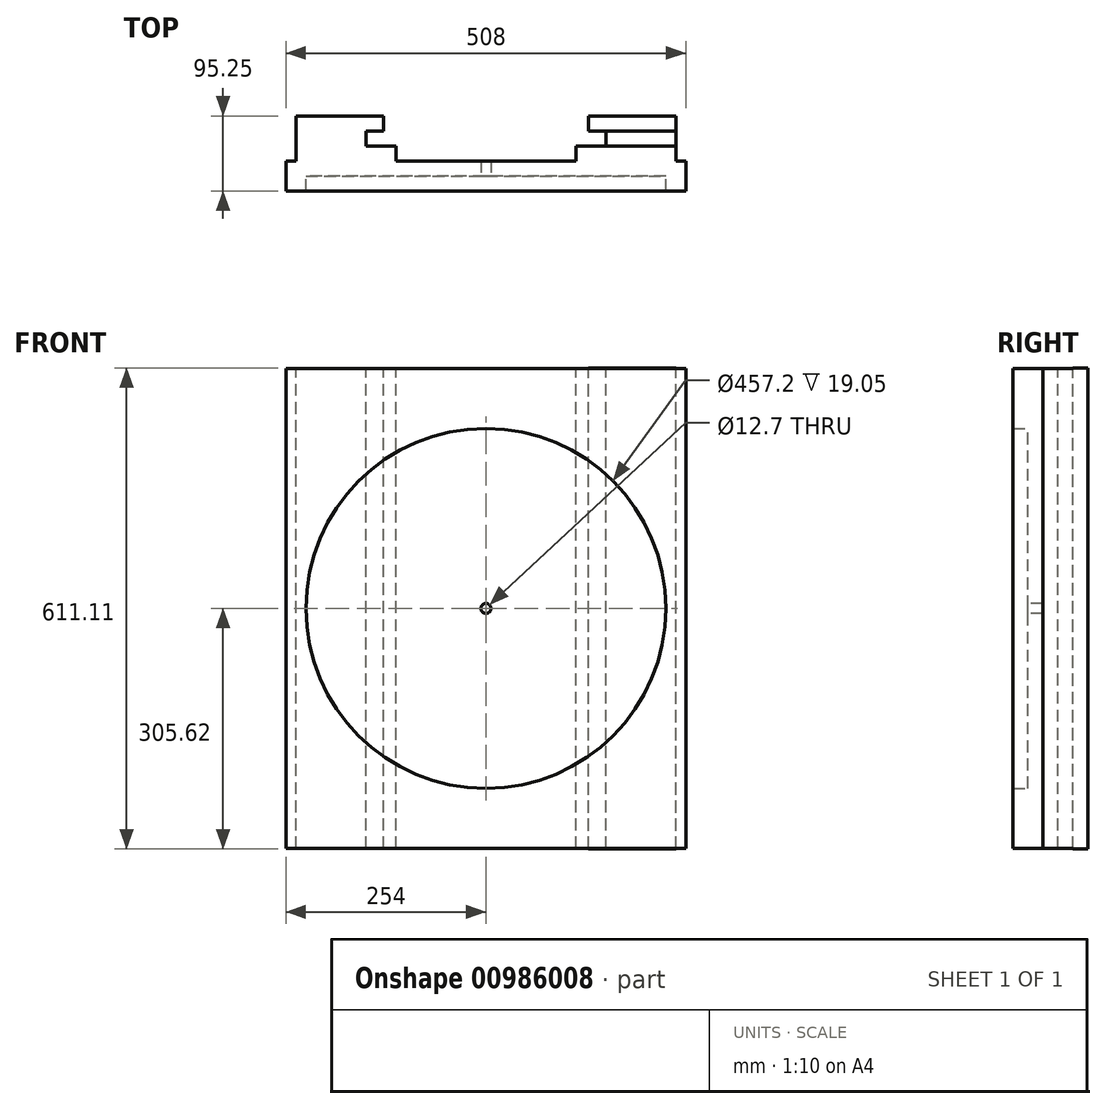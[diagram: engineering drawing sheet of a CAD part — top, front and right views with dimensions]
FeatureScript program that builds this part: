
annotation { "Feature Type Name" : "Feature", "Feature Type Description" : "" }
export const myFeature = defineFeature(function(context is Context, id is Id, definition is map)
    precondition{}
    {
        {
            var Q0;
            Q0=qCreatedBy(makeId("Front.planeOp"),FACE);
            var sketch = newSketch(context, id + "F0", { "sketchPlane" : qUnion([Q0])});
            skLineSegment(sketch, "E0.bottom", {"start": v(254, -304.8) * mm, "end": v(-254, -304.8) * mm});
            skLineSegment(sketch, "E0.top", {"start": v(254, 304.8) * mm, "end": v(-254, 304.8) * mm});
            skLineSegment(sketch, "E0.left", {"start": v(254, -304.8) * mm, "end": v(254, 304.8) * mm});
            skLineSegment(sketch, "E0.right", {"start": v(-254, -304.8) * mm, "end": v(-254, 304.8) * mm});
            skPoint(sketch, "E0.middle", {"position": v(0, 0) * mm});
            skSolve(sketch);
        }
        {
            var Q0;
            Q0 = qSketchRegion(id + "F0", true);
            extrude(context, id + "F1", {"entities" : qUnion([Q0]), "depth" : 19.05 * mm, "offsetDistance" : 25.4 * mm});
        }
        {
            var Q0;
            Q0=makeQuery(id+"F1.opExtrude","CAP_FACE",FACE,{"disambiguationData":[OSD([sQuery(id+"F0.wireOp",EDGE,"E0.bottom"),sQuery(id+"F0.wireOp",EDGE,"E0.top"),sQuery(id+"F0.wireOp",EDGE,"E0.left"),sQuery(id+"F0.wireOp",EDGE,"E0.right")])],"isStart":true});
            var sketch = newSketch(context, id + "F2", { "sketchPlane" : qUnion([Q0])});
            skLineSegment(sketch, "E1.bottom", {"start": v(-241.3, -304.8) * mm, "end": v(-114.3, -304.8) * mm});
            skLineSegment(sketch, "E1.top", {"start": v(-241.3, 304.8) * mm, "end": v(-114.3, 304.8) * mm});
            skLineSegment(sketch, "E1.left", {"start": v(-241.3, -304.8) * mm, "end": v(-241.3, 304.8) * mm});
            skLineSegment(sketch, "E1.right", {"start": v(-114.3, -304.8) * mm, "end": v(-114.3, 304.8) * mm});
            skLineSegment(sketch, "E2.bottom", {"start": v(114.3, -304.8) * mm, "end": v(241.3, -304.8) * mm});
            skLineSegment(sketch, "E2.top", {"start": v(114.3, 304.8) * mm, "end": v(241.3, 304.8) * mm});
            skLineSegment(sketch, "E2.left", {"start": v(114.3, -304.8) * mm, "end": v(114.3, 304.8) * mm});
            skLineSegment(sketch, "E2.right", {"start": v(241.3, -304.8) * mm, "end": v(241.3, 304.8) * mm});
            skSolve(sketch);
        }
        {
            var Q0;
            Q0=makeQuery(id+"F2.imprint","IMPRINT",FACE,{"disambiguationData":[TD([[makeQuery(id+"F2.imprint","IMPRINT",EDGE,{"derivedFrom":sQuery(id+"F2.wireOp",EDGE,"E2.bottom")}),1.0]])]});
            var Q1;
            Q1=makeQuery(id+"F2.imprint","IMPRINT",FACE,{"disambiguationData":[TD([[makeQuery(id+"F2.imprint","IMPRINT",EDGE,{"derivedFrom":sQuery(id+"F2.wireOp",EDGE,"E1.bottom")}),1.0]])]});
            extrude(context, id + "F3", {"entities" : qUnion([Q0, Q1]), "operationType" : NewBodyOperationType.ADD, "depth" : 19.05 * mm, "offsetDistance" : 25.4 * mm});
        }
        {
            var Q0;
            Q0=makeQuery(id+"F3.opExtrude","CAP_FACE",FACE,{"disambiguationData":[OSD([sQuery(id+"F2.wireOp",EDGE,"E2.bottom"),sQuery(id+"F2.wireOp",EDGE,"E2.top"),sQuery(id+"F2.wireOp",EDGE,"E2.left"),sQuery(id+"F2.wireOp",EDGE,"E2.right")])],"isStart":false});
            var sketch = newSketch(context, id + "F4", { "sketchPlane" : qUnion([Q0])});
            skLineSegment(sketch, "E3.bottom", {"start": v(241.3, -304.8) * mm, "end": v(152.4, -304.8) * mm});
            skLineSegment(sketch, "E3.top", {"start": v(241.3, 304.8) * mm, "end": v(152.4, 304.8) * mm});
            skLineSegment(sketch, "E3.left", {"start": v(241.3, -304.8) * mm, "end": v(241.3, 304.8) * mm});
            skLineSegment(sketch, "E3.right", {"start": v(152.4, -304.8) * mm, "end": v(152.4, 304.8) * mm});
            skLineSegment(sketch, "E4.bottom", {"start": v(-152.4, -304.78) * mm, "end": v(-241.3, -304.78) * mm});
            skLineSegment(sketch, "E4.top", {"start": v(-152.4, 304.82) * mm, "end": v(-241.3, 304.82) * mm});
            skLineSegment(sketch, "E4.left", {"start": v(-152.4, -304.78) * mm, "end": v(-152.4, 304.82) * mm});
            skLineSegment(sketch, "E4.right", {"start": v(-241.3, -304.78) * mm, "end": v(-241.3, 304.82) * mm});
            skSolve(sketch);
        }
        {
            var Q0;
            Q0=makeQuery(id+"F4.imprint","IMPRINT",FACE,{"disambiguationData":[TD([[makeQuery(id+"F4.imprint","IMPRINT",EDGE,{"derivedFrom":sQuery(id+"F4.wireOp",EDGE,"E3.bottom")}),1.0]])]});
            var Q1;
            Q1=makeQuery(id+"F4.imprint","IMPRINT",FACE,{"disambiguationData":[TD([[makeQuery(id+"F4.imprint","IMPRINT",EDGE,{"derivedFrom":sQuery(id+"F4.wireOp",EDGE,"E4.bottom")}),-1.0]])]});
            extrude(context, id + "F5", {"entities" : qUnion([Q0, Q1]), "operationType" : NewBodyOperationType.ADD, "depth" : 19.05 * mm, "offsetDistance" : 25.4 * mm});
        }
        {
            var Q0;
            Q0=makeQuery(id+"F5.opExtrude","CAP_FACE",FACE,{"disambiguationData":[OSD([sQuery(id+"F4.wireOp",EDGE,"E3.bottom"),sQuery(id+"F4.wireOp",EDGE,"E3.top"),sQuery(id+"F4.wireOp",EDGE,"E3.left"),sQuery(id+"F4.wireOp",EDGE,"E3.right")])],"isStart":false});
            var sketch = newSketch(context, id + "F6", { "sketchPlane" : qUnion([Q0])});
            skPoint(sketch, "E5.firstSnap0", {"position": v(196.85, -304.8) * mm});
            skLineSegment(sketch, "E5.bottom", {"start": v(130.18, -304.8) * mm, "end": v(241.3, -304.8) * mm});
            skLineSegment(sketch, "E5.top", {"start": v(130.17, 304.8) * mm, "end": v(241.3, 304.8) * mm});
            skLineSegment(sketch, "E5.left", {"start": v(130.18, -304.8) * mm, "end": v(130.17, 304.8) * mm});
            skLineSegment(sketch, "E5.right", {"start": v(241.3, -304.8) * mm, "end": v(241.3, 304.8) * mm});
            skLineSegment(sketch, "E6.bottom", {"start": v(-130.17, -305.62) * mm, "end": v(-241.3, -305.62) * mm});
            skLineSegment(sketch, "E6.top", {"start": v(-130.18, 305.49) * mm, "end": v(-241.3, 305.49) * mm});
            skLineSegment(sketch, "E6.left", {"start": v(-130.17, -305.62) * mm, "end": v(-130.18, 305.49) * mm});
            skLineSegment(sketch, "E6.right", {"start": v(-241.3, -305.62) * mm, "end": v(-241.3, 305.49) * mm});
            skSolve(sketch);
        }
        {
            var Q0;
            {var subQ0=sQuery(id+"F6.wireOp",EDGE,"E5.right");Q0=makeQuery(id+"F6.imprint","IMPRINT",FACE,{"disambiguationData":[TD([[makeQuery(id+"F6.imprint","IMPRINT",EDGE,{"derivedFrom":subQ0}),1.0]])]});}
            var Q1;
            {var subQ2=sQuery(id+"F6.wireOp",EDGE,"E5.left");Q1=makeQuery(id+"F6.imprint","IMPRINT",FACE,{"disambiguationData":[TD([[makeQuery(id+"F6.imprint","IMPRINT",EDGE,{"derivedFrom":subQ2}),-1.0]])]});}
            var Q2;
            Q2=makeQuery(id+"F6.imprint","IMPRINT",FACE,{"disambiguationData":[TD([[makeQuery(id+"F6.imprint","IMPRINT",EDGE,{"derivedFrom":sQuery(id+"F6.wireOp",EDGE,"E6.bottom")}),-1.0]])]});
            extrude(context, id + "F7", {"entities" : qUnion([Q0, Q1, Q2]), "operationType" : NewBodyOperationType.ADD, "depth" : 19.05 * mm, "offsetDistance" : 25.4 * mm});
        }
        {
            var Q0;
            Q0=makeQuery(id+"F1.opExtrude","CAP_FACE",FACE,{"disambiguationData":[OSD([sQuery(id+"F0.wireOp",EDGE,"E0.bottom"),sQuery(id+"F0.wireOp",EDGE,"E0.top"),sQuery(id+"F0.wireOp",EDGE,"E0.left"),sQuery(id+"F0.wireOp",EDGE,"E0.right")])],"isStart":false});
            var sketch = newSketch(context, id + "F8", { "sketchPlane" : qUnion([Q0])});
            skCircle(sketch, "E7", {"center": v(0, 0) * mm, "radius": 228.6 * mm});
            skCircle(sketch, "E8", {"center": v(0, 0) * mm, "radius": 6.35 * mm});
            skSolve(sketch);
        }
        {
            var Q0;
            Q0=makeQuery(id+"F8.imprint","IMPRINT",FACE,{"disambiguationData":[TD([[makeQuery(id+"F8.imprint","IMPRINT",EDGE,{"derivedFrom":sQuery(id+"F8.wireOp",EDGE,"E7")}),-1.0]])]});
            extrude(context, id + "F9", {"entities" : qUnion([Q0]), "operationType" : NewBodyOperationType.ADD, "depth" : 19.05 * mm, "offsetDistance" : 25.4 * mm});
        }
        {
            var Q0;
            Q0=sQuery(id+"F8.wireOp",VERTEX,"E7.center");
            var Q1;
            Q1=makeQuery(id+"F1.opExtrude","SWEPT_BODY",BODY,{"disambiguationData":[OSD([sQuery(id+"F0.wireOp",EDGE,"E0.bottom"),sQuery(id+"F0.wireOp",EDGE,"E0.top"),sQuery(id+"F0.wireOp",EDGE,"E0.left"),sQuery(id+"F0.wireOp",EDGE,"E0.right")])]});
            hole(context, id + "F10", {"style" : HoleStyle.SIMPLE, "endStyle" : HoleEndStyle.THROUGH, "holeDiameter" : 12.7 * mm, "majorDiameter" : 6.35 * mm, "isTappedThrough" : true, "tappedDepth" : 12.7 * mm, "tapClearance" : 3, "locations" : qUnion([Q0]), "scope" : qUnion([Q1])});
        }
    });
